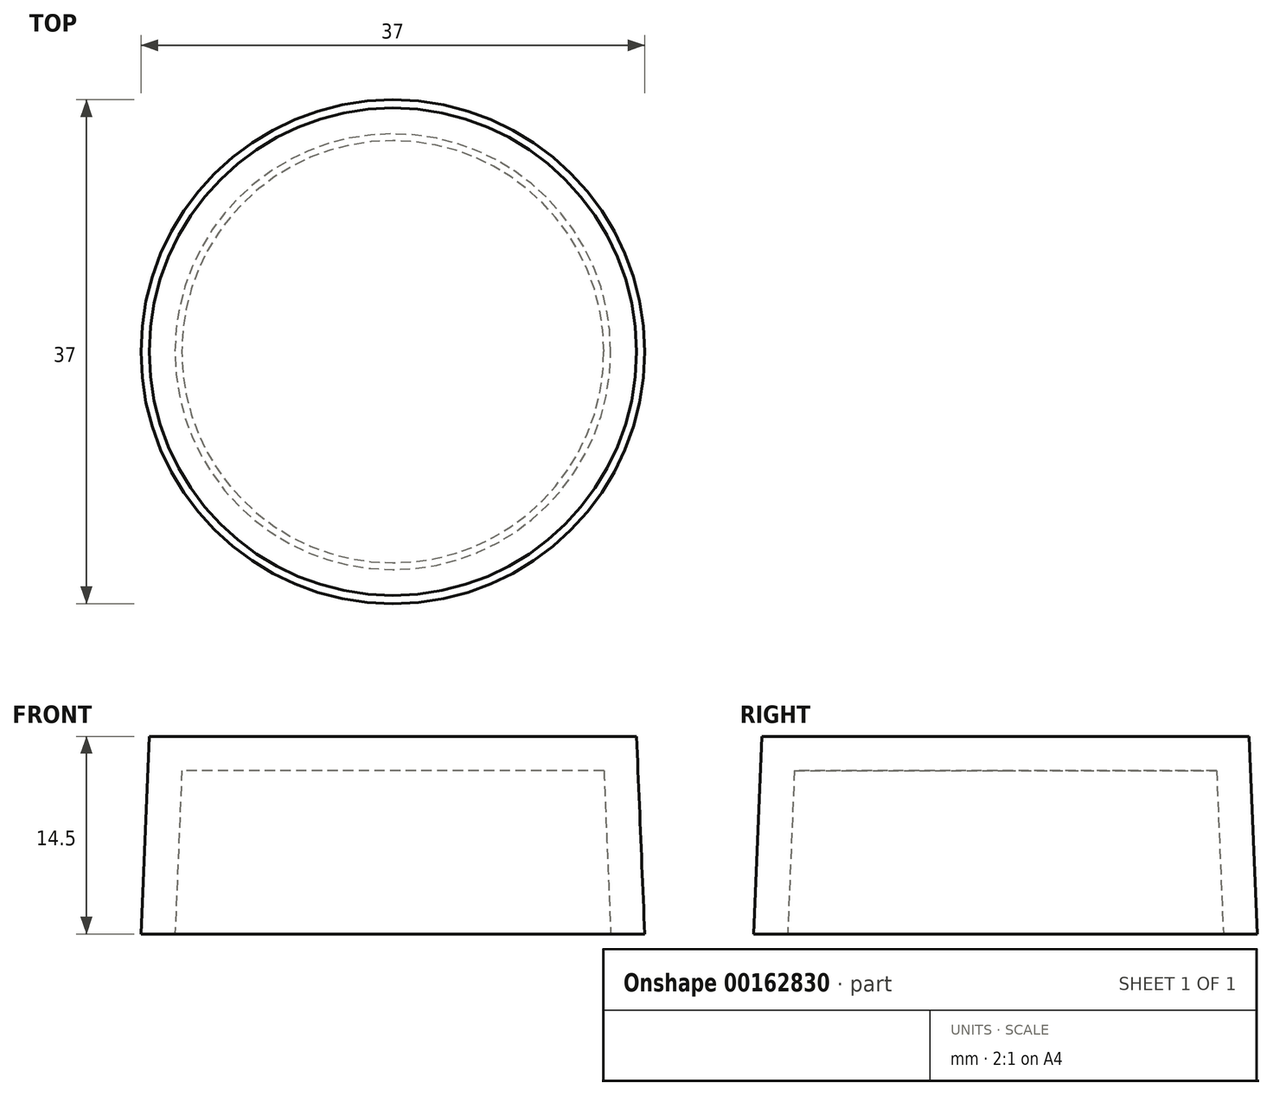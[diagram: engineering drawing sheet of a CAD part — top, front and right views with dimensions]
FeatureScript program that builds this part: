
annotation { "Feature Type Name" : "Feature", "Feature Type Description" : "" }
export const myFeature = defineFeature(function(context is Context, id is Id, definition is map)
    precondition{}
    {
        {
            var Q0;
            Q0=qCreatedBy(makeId("Top.planeOp"),FACE);
            var sketch = newSketch(context, id + "F0", { "sketchPlane" : qUnion([Q0])});
            skCircle(sketch, "E0", {"center": v(0, 0) * mm, "radius": 16 * mm});
            skSolve(sketch);
        }
        {
            var Q0;
            Q0=qCreatedBy(makeId("Top.planeOp"),FACE);
            cPlane(context, id + "F1", {"entities" : qUnion([Q0]), "cplaneType" : CPlaneType.OFFSET, "offset" : 12 * mm, "width" : 150 * mm, "height" : 150 * mm});
        }
        {
            var Q0;
            Q0=qCreatedBy(id+"F1.planeOp",FACE);
            var sketch = newSketch(context, id + "F2", { "sketchPlane" : qUnion([Q0])});
            skCircle(sketch, "E1", {"center": v(0, 0) * mm, "radius": 15.5 * mm});
            skSolve(sketch);
        }
        {
            var Q0;
            Q0=makeQuery(id+"F0.imprint","IMPRINT",FACE,{"disambiguationData":[TD([[makeQuery(id+"F0.imprint","IMPRINT",EDGE,{"derivedFrom":sQuery(id+"F0.wireOp",EDGE,"E0")}),1.0]])]});
            var Q1;
            Q1=makeQuery(id+"F2.imprint","IMPRINT",FACE,{"disambiguationData":[TD([[makeQuery(id+"F2.imprint","IMPRINT",EDGE,{"derivedFrom":sQuery(id+"F2.wireOp",EDGE,"E1")}),1.0]])]});
            loft(context, id + "F3", {"sheetProfilesArray" : [{ "sheetProfileEntities" : qUnion([Q0]) }, { "sheetProfileEntities" : qUnion([Q1]) }]});
        }
        {
            var Q0;
            Q0=makeQuery(id+"F3.opLoft","CAP_FACE",FACE,{"disambiguationData":[OSD([makeQuery(id+"F0.imprint","IMPRINT",FACE,{"disambiguationData":[TD([[makeQuery(id+"F0.imprint","IMPRINT",EDGE,{"derivedFrom":sQuery(id+"F0.wireOp",EDGE,"E0")}),1.0]])]})])],"isStart":true});
            shell(context, id + "F4", {"entities" : qUnion([Q0]), "thickness" : 2.5 * mm, "oppositeDirection" : true});
        }
    });
